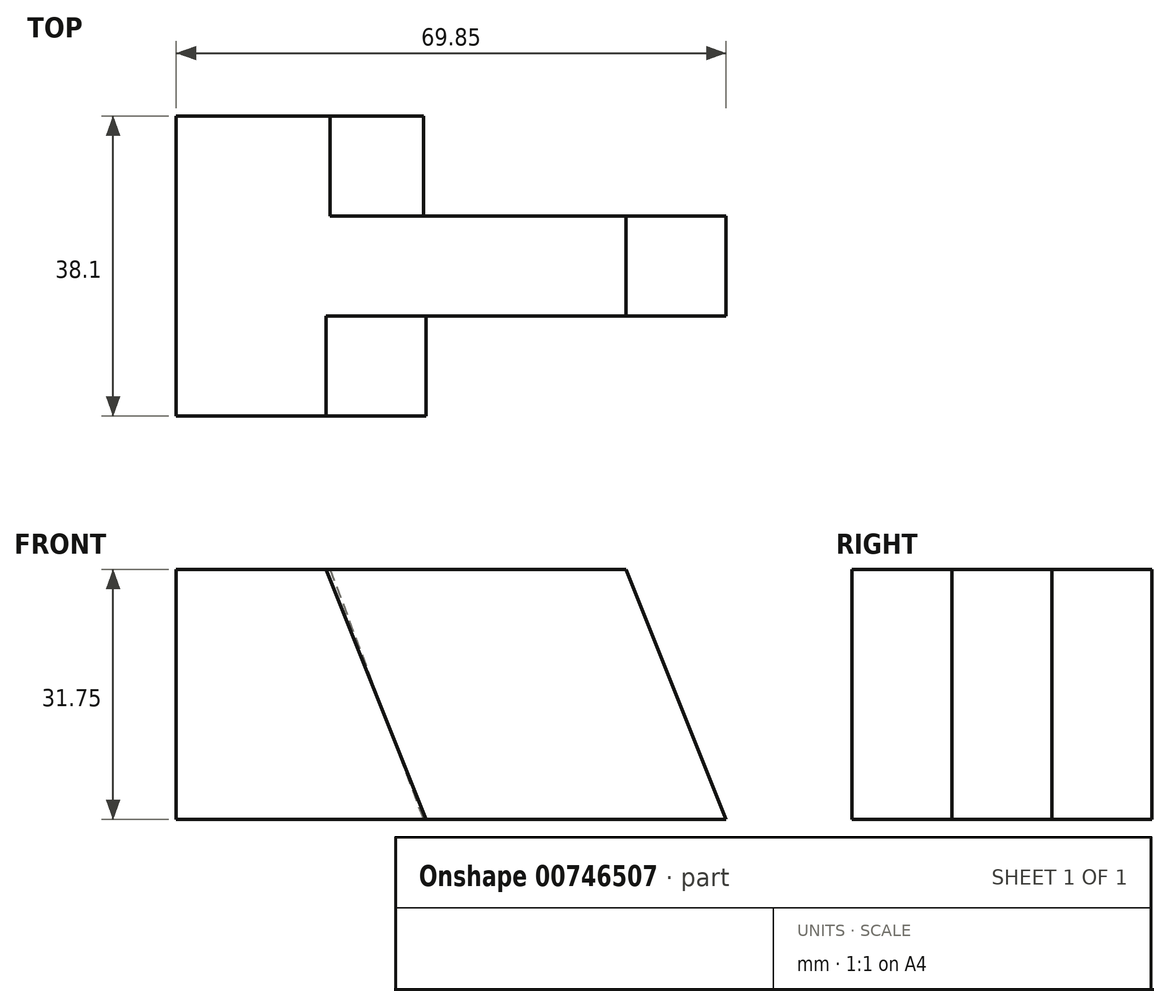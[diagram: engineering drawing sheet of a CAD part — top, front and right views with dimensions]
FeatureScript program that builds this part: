
annotation { "Feature Type Name" : "Feature", "Feature Type Description" : "" }
export const myFeature = defineFeature(function(context is Context, id is Id, definition is map)
    precondition{}
    {
        {
            var Q0;
            Q0=qCreatedBy(makeId("Top.planeOp"),FACE);
            var sketch = newSketch(context, id + "F0", { "sketchPlane" : qUnion([Q0])});
            skLineSegment(sketch, "E0", {"start": v(0, 0) * mm, "end": v(0, 38.1) * mm});
            skLineSegment(sketch, "E1", {"start": v(0, 38.1) * mm, "end": v(31.4, 38.1) * mm});
            skLineSegment(sketch, "E2", {"start": v(31.4, 38.1) * mm, "end": v(31.4, 25.4) * mm});
            skLineSegment(sketch, "E3", {"start": v(31.4, 25.4) * mm, "end": v(69.85, 25.4) * mm});
            skLineSegment(sketch, "E4", {"start": v(69.85, 25.4) * mm, "end": v(69.85, 12.7) * mm});
            skLineSegment(sketch, "E5", {"start": v(69.85, 12.7) * mm, "end": v(31.75, 12.7) * mm});
            skLineSegment(sketch, "E6", {"start": v(31.75, 12.7) * mm, "end": v(31.75, 0) * mm});
            skLineSegment(sketch, "E7", {"start": v(31.75, 0) * mm, "end": v(0, 0) * mm});
            skSolve(sketch);
        }
        {
            var Q0;
            Q0=makeQuery(id+"F0.imprint","IMPRINT",FACE,{"disambiguationData":[TD([[makeQuery(id+"F0.imprint","IMPRINT",EDGE,{"derivedFrom":sQuery(id+"F0.wireOp",EDGE,"E0")}),-1.0]])]});
            extrude(context, id + "F1", {"entities" : qUnion([Q0]), "depth" : 31.75 * mm, "offsetDistance" : 25.4 * mm});
        }
        {
            var Q0;
            Q0=makeQuery(id+"F1.opExtrude","SWEPT_FACE",FACE,{"disambiguationData":[OSD([sQuery(id+"F0.wireOp",EDGE,"E5")])]});
            var sketch = newSketch(context, id + "F2", { "sketchPlane" : qUnion([Q0])});
            skLineSegment(sketch, "E8", {"start": v(57.15, 31.75) * mm, "end": v(69.85, 0) * mm});
            skLineSegment(sketch, "E9", {"start": v(69.85, 0) * mm, "end": v(69.85, 31.75) * mm});
            skLineSegment(sketch, "E10", {"start": v(69.85, 31.75) * mm, "end": v(57.15, 31.75) * mm});
            skSolve(sketch);
        }
        {
            var Q0;
            Q0=makeQuery(id+"F2.imprint","IMPRINT",FACE,{"disambiguationData":[TD([[makeQuery(id+"F2.imprint","IMPRINT",EDGE,{"derivedFrom":sQuery(id+"F2.wireOp",EDGE,"E8")}),1.0]])]});
            extrude(context, id + "F3", {"entities" : qUnion([Q0]), "operationType" : NewBodyOperationType.REMOVE, "oppositeDirection" : true, "depth" : 25.4 * mm, "offsetDistance" : 25.4 * mm});
        }
        {
            var Q0;
            Q0=makeQuery(id+"F1.opExtrude","SWEPT_FACE",FACE,{"disambiguationData":[OSD([sQuery(id+"F0.wireOp",EDGE,"E7")])]});
            var sketch = newSketch(context, id + "F4", { "sketchPlane" : qUnion([Q0])});
            skLineSegment(sketch, "E11", {"start": v(19.05, 31.75) * mm, "end": v(31.75, 0) * mm});
            skLineSegment(sketch, "E12", {"start": v(31.75, 0) * mm, "end": v(31.75, 31.75) * mm});
            skLineSegment(sketch, "E13", {"start": v(31.75, 31.75) * mm, "end": v(19.05, 31.75) * mm});
            skSolve(sketch);
        }
        {
            var Q0;
            Q0=makeQuery(id+"F4.imprint","IMPRINT",FACE,{"disambiguationData":[TD([[makeQuery(id+"F4.imprint","IMPRINT",EDGE,{"derivedFrom":sQuery(id+"F4.wireOp",EDGE,"E11")}),1.0]])]});
            extrude(context, id + "F5", {"entities" : qUnion([Q0]), "operationType" : NewBodyOperationType.REMOVE, "oppositeDirection" : true, "depth" : 12.7 * mm, "offsetDistance" : 25.4 * mm});
        }
        {
            var Q0;
            Q0=makeQuery(id+"F1.opExtrude","SWEPT_FACE",FACE,{"disambiguationData":[OSD([sQuery(id+"F0.wireOp",EDGE,"E1")])]});
            var sketch = newSketch(context, id + "F6", { "sketchPlane" : qUnion([Q0])});
            skLineSegment(sketch, "E14", {"start": v(-19.56, 31.75) * mm, "end": v(-31.4, 0) * mm});
            skLineSegment(sketch, "E15", {"start": v(-31.4, 0) * mm, "end": v(-31.4, 31.75) * mm});
            skLineSegment(sketch, "E16", {"start": v(-32.23, 32.52) * mm, "end": v(-19.56, 31.75) * mm});
            skSolve(sketch);
        }
        {
            var Q0;
            {var subQ0=sQuery(id+"F6.wireOp",EDGE,"E14");Q0=makeQuery(id+"F6.imprint","IMPRINT",FACE,{"disambiguationData":[TD([[makeQuery(id+"F6.imprint","IMPRINT",EDGE,{"derivedFrom":subQ0}),-1.0]])]});}
            extrude(context, id + "F7", {"entities" : qUnion([Q0]), "operationType" : NewBodyOperationType.REMOVE, "oppositeDirection" : true, "depth" : 12.7 * mm, "offsetDistance" : 25.4 * mm});
        }
    });
